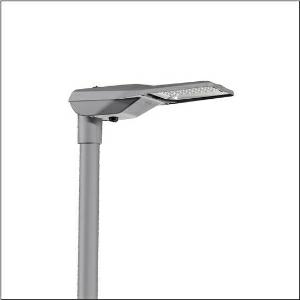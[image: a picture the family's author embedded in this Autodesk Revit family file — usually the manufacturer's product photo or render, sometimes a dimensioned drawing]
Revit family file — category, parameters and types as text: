
# Revit family: streetlight_sl_21_iq_mini___st1_0a_5xe2d41y08jb_7656
name_source: partatom
category: Lighting Fixtures
units: mm (PartAtom-declared; Revit-internal decimal feet)

## family parameters
Cut with Voids When Loaded = No
Host = Face
Light Source = No
Part Type = Normal
Room Calculation Point = No
Round Connector Dimension = Use Diameter
Shared = No

## types (1)
- --- (1 x LED, 11600 lm, 72.5 W, 4000K)
    Apparent Load = 73 VA
    CIE Flux Codes = 40 73 97 100 100
    Color Rendering = 70
    Color Temperature = 4000K
    Default Elevation = 1800 mm
    Description = Streetlight SL 21 iQ mini, mast luminaire, primary light control with lens, of PMMA, primary optical cover: cover, of toughened safety glass, transparent, light distribution: ST1.0a, light emission: direct distribution, primary light characteristic: asymmetric, installation type: post-top, side-entry, LED, High Power LED, rated luminous flux: 11.600lm, luminous efficacy: 160lm/W, light colour: 740, colour temperature: 4000K, control gear: iQ-Street Remote, D4i with power reduction, control: pre-setting: logarithmic dimming characteristic, Street-Remote, Auto-Match, Temp-Guard, Lumen-Switch, Night-Set, Smart-Wire, Light-Fading, Desk-Remote (wireless, voltage-free reading and setting of iQ features in the workshop via application-optimized NFC function/RFID function), optimised constant luminous flux control (CLO 2.0), mains connection: 220..240V, AC, 50/60Hz, start of lifetime: 73W, end of service life: 76W, reduction: 33W, luminaire housing, of diecast aluminium, powder-coated, SITECO metallic grey (DB 702S), corrosivity category C5 high according to DIN EN ISO 12944, please order mast flange separately, inclination adjustable: 0°, 5°, 10°, 15°, sealing non-destructively replaceable, multi-level sealing system, length: 628mm, width: 235mm, height: 110mm, mast flange for spigot size: 42mm (side-entry): 5XC10008XM4, 60/48mm (side-entry/post-top): 5XC10108XM2, 76/60mm (side-entry/post-top): 5XC10108XM1, mounting height: 4..8m, Smart Interface below and above, protection rating (complete): IP66, insulation class (complete): insulation class II (safety insulation), certification: CE, ENEC, ENEC+, VDE, impact resistance: IK10, permissible operating ambient temperature for outdoor applications: -40..+50°C, standard-compliant lighting for roads and squares, packaging unit: 1 piece

Light Distribution: ST1.0a
    Height = 110 mm
    Lamp = 1 x LED
    Lamp Light Flux = 11600 lm
    Lamp Power = 72.5 W
    Lamp count = 1
    Length = 625 mm
    Luminous efficacy = 160 lm/W
    Manufacturer = Siteco
    ModVariant = No
    Model = 5XE2D41Y08JB
    Number of Poles = 1
    OnlyDefault = Yes
    Power Factor = 1
    Product Name = Streetlight SL 21 iQ mini | ST1.0a
    Product group = mast luminaire | pylon top
    ProductGroupID = 6100
    Protection Class = Protection class II
    Protection Degree = IP 66
    RLX_Detail_Level = 1
    RLX_Emergency_Light_Flux = 0 lm
    RLX_Emergency_Type = 0
    RLX_Emergency_Type_DB = No
    RlxData = <blob elided: 92709 chars, md5=164d723a>
    Socket = socket
    Standby Power = 0 W
    System Light Flux = 11600 lm
    System Power = 73 W
    Type Comments = factory setting: luminous flux: 100 % | dim-lin: 254 | 755 mA
    Type Image = l_1003514.jpg
    URL = http://relux.com
    VarID = @adj_114119
    Voltage = 0 V
    Weight = 0.00 kg
    Width = 234 mm

## geometry (parser evidence)
native form markers: Blend x4, Sweep x11
no freeform markers — native parametric forms only
